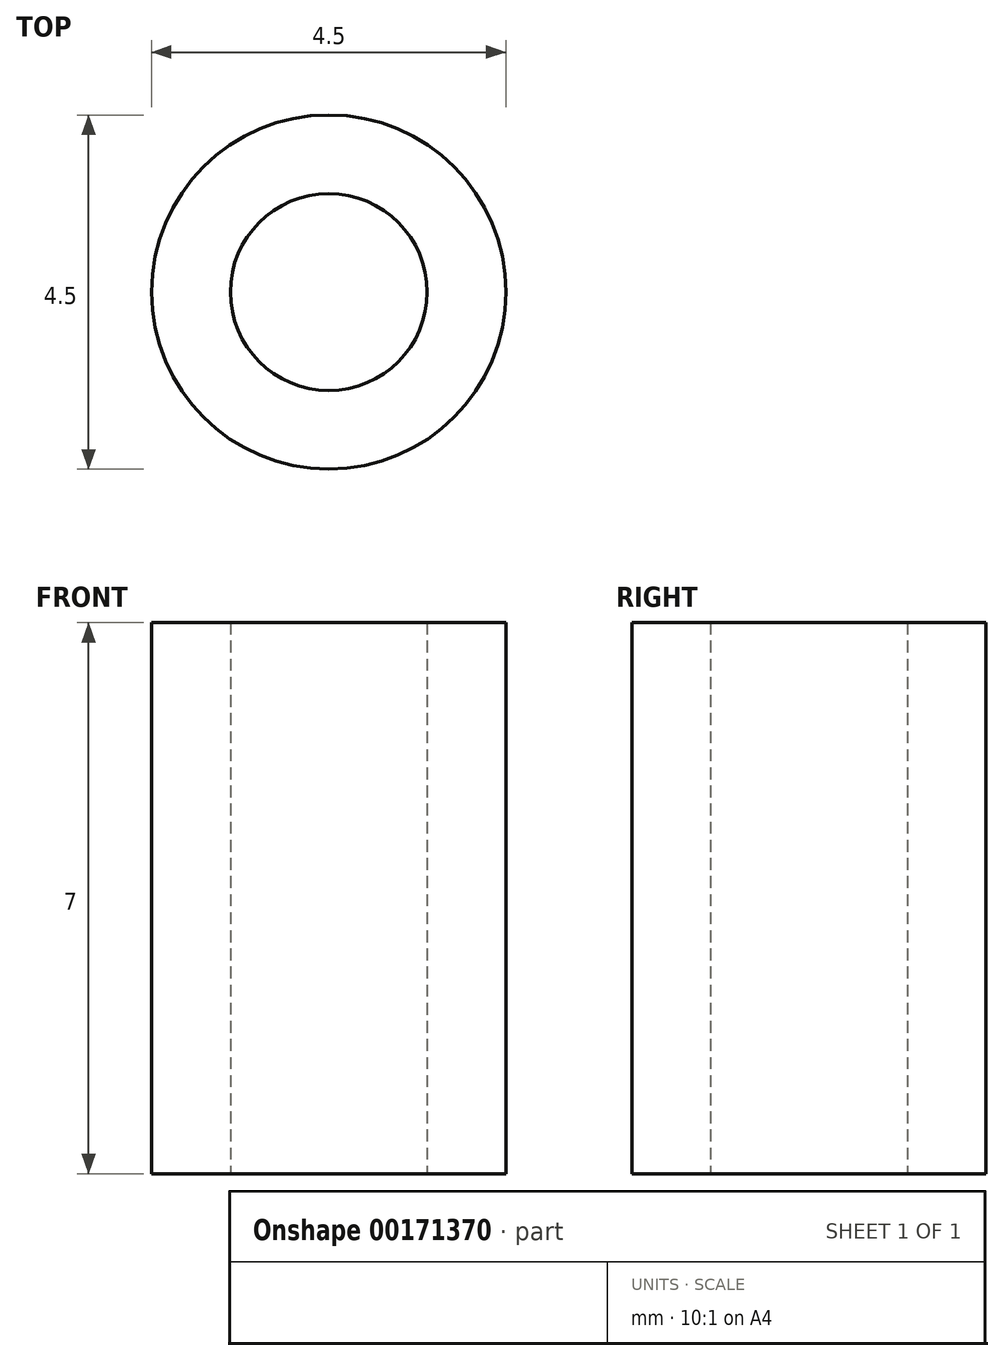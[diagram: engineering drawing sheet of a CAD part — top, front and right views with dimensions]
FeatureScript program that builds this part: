
annotation { "Feature Type Name" : "Feature", "Feature Type Description" : "" }
export const myFeature = defineFeature(function(context is Context, id is Id, definition is map)
    precondition{}
    {
        {
            var Q0;
            Q0=qCreatedBy(makeId("Top.planeOp"),FACE);
            var sketch = newSketch(context, id + "F0", { "sketchPlane" : qUnion([Q0])});
            skCircle(sketch, "E0", {"center": v(0, 0) * mm, "radius": 2.25 * mm});
            skCircle(sketch, "E1", {"center": v(0, 0) * mm, "radius": 1.25 * mm});
            skSolve(sketch);
        }
        {
            var Q0;
            Q0 = qSketchRegion(id + "F0", true);
            extrude(context, id + "F1", {"entities" : qUnion([Q0]), "depth" : 7 * mm});
        }
    });
